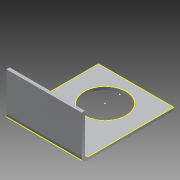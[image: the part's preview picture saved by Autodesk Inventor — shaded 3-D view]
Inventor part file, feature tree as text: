
AUTODESK INVENTOR PART (.ipt)
format: ipt  version: 2013 (Build 170138000, 138)  size: 143,360 bytes
history: native  units: in
note: dims shown in document units (in); Inventor stores cm internally (conversion verified against a paired STEP export)
features: sketch x7, sheet_metal_op x6, other x4, extrude x2
ambient origin geometry x8: Origin, YZ Plane, XZ Plane, XY Plane, X Axis, Y Axis, Z Axis, Center Point
bodies: Solid1 (feature_tree)
feature tree (19):
  sheet_metal_op  "Face1"
  sheet_metal_op  "Flange1"
  sheet_metal_op  "Face2"
  extrude  "Extrusion1"  Depth=2.0in
  extrude  "Extrusion2"  Depth=1.0in
  sketch  "Sketch7"  dims[d8=0.125in d9=1.5in d10=90.0deg d11=0.125in d12=0.5in d13=0.125in d14=0.125in d15=0.75in d16=0.125in d17=0.125in d18=0.0625in d19=0.25in d20=0.125in d21=0.25in d22=0.0in d23=0.125in d24=0.0in d25=1.222in d26=1.647in d27=0.125in d28=0.0in]
  sketch  "Sketch1"  dims[d0=1.469in d1=2.0in]
  other  "Plate1"
  sketch  "Sketch2"  dims[d2=1.5in d3=1.0in]
  other  "Plate2"
  sheet_metal_op  "Bend1"
  sheet_metal_op  "Corner1"
  sketch  "Sketch3"  dims[d4=0.125in]
  other  "Plate3"
  sheet_metal_op  "Bend2"
  sketch  "Sketch4"  dims[d5=0.125in]
  sketch  "Sketch5"  dims[d6=0.0625in]
  sketch  "Sketch6"  dims[d7=0.25in]
  other  "Cut1"
